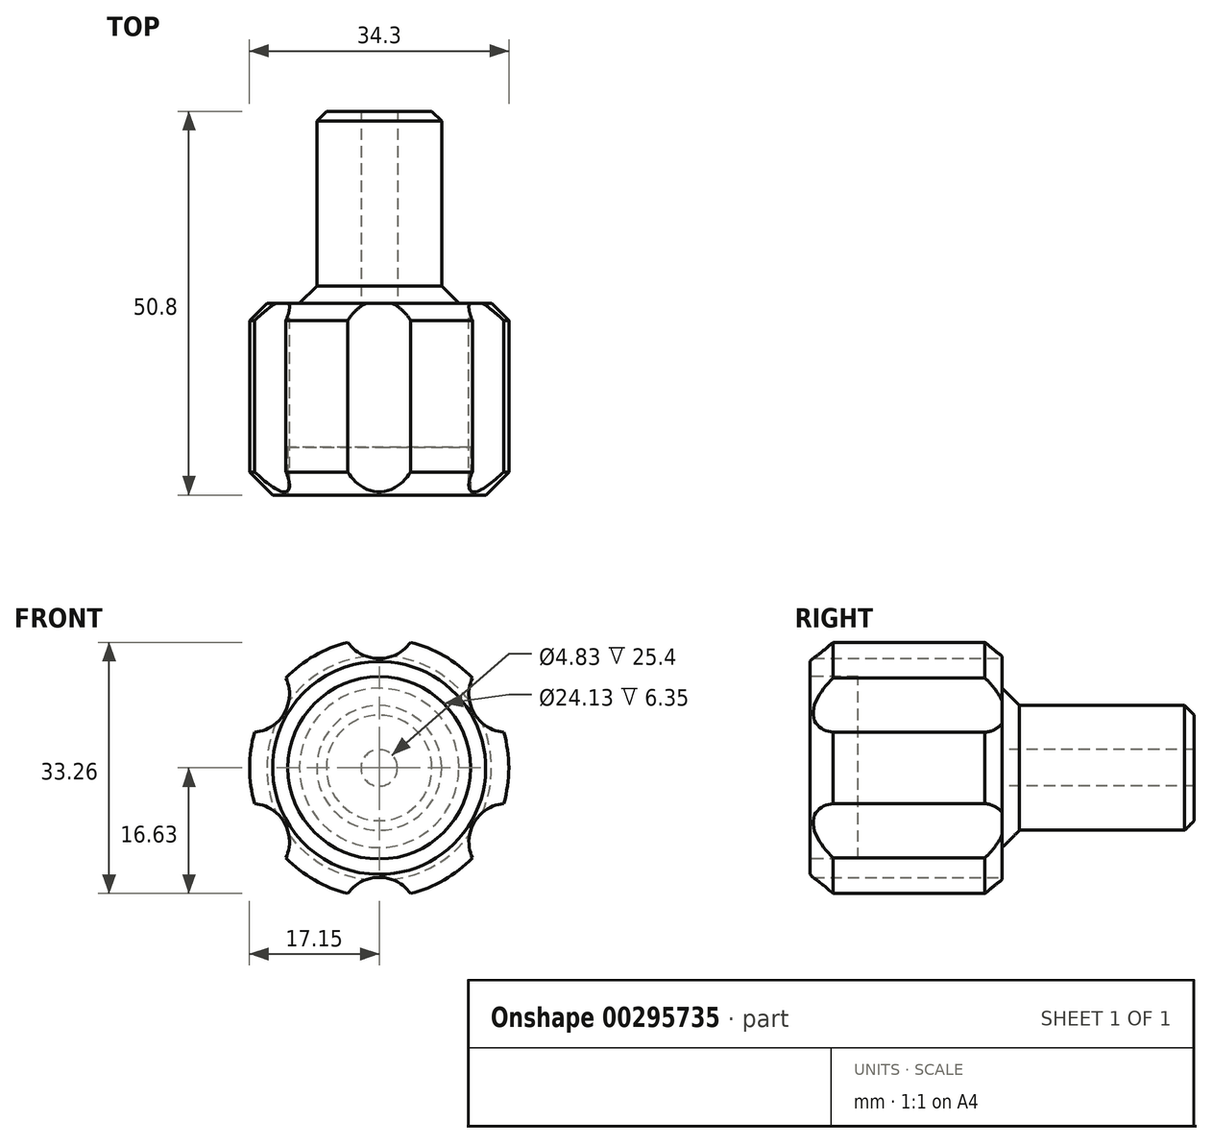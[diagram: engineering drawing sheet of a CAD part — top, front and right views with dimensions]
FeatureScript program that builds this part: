
annotation { "Feature Type Name" : "Feature", "Feature Type Description" : "" }
export const myFeature = defineFeature(function(context is Context, id is Id, definition is map)
    precondition{}
    {
        {
            var Q0;
            Q0=qCreatedBy(makeId("Front.planeOp"),FACE);
            var sketch = newSketch(context, id + "F0", { "sketchPlane" : qUnion([Q0])});
            skCircle(sketch, "E0", {"center": v(0, 0) * mm, "radius": 17.15 * mm});
            skSolve(sketch);
        }
        {
            var Q0;
            Q0=qCreatedBy(makeId("Front.planeOp"),FACE);
            var sketch = newSketch(context, id + "F1", { "sketchPlane" : qUnion([Q0])});
            skCircle(sketch, "E1", {"center": v(0, 0) * mm, "radius": 8.26 * mm});
            skSolve(sketch);
        }
        {
            var Q0;
            Q0=qCreatedBy(makeId("Front.planeOp"),FACE);
            var sketch = newSketch(context, id + "F2", { "sketchPlane" : qUnion([Q0])});
            skCircle(sketch, "E2", {"center": v(0, 0) * mm, "radius": 2.41 * mm});
            skSolve(sketch);
        }
        {
            var Q0;
            Q0=qCreatedBy(makeId("Front.planeOp"),FACE);
            cPlane(context, id + "F3", {"entities" : qUnion([Q0]), "cplaneType" : CPlaneType.OFFSET, "offset" : 25.4 * mm, "width" : 152.4 * mm, "height" : 152.4 * mm});
        }
        {
            var Q0;
            Q0=qCreatedBy(id+"F3.planeOp",FACE);
            var sketch = newSketch(context, id + "F4", { "sketchPlane" : qUnion([Q0])});
            skCircle(sketch, "E3", {"center": v(0, 0) * mm, "radius": 12.07 * mm});
            skSolve(sketch);
        }
        {
            var Q0;
            Q0 = qSketchRegion(id + "F0", true);
            extrude(context, id + "F5", {"entities" : qUnion([Q0]), "depth" : 25.4 * mm});
        }
        {
            var Q0;
            Q0=makeQuery(id+"F1.imprint","IMPRINT",FACE,{"disambiguationData":[TD([[makeQuery(id+"F1.imprint","IMPRINT",EDGE,{"derivedFrom":sQuery(id+"F1.wireOp",EDGE,"E1")}),1.0]])]});
            extrude(context, id + "F6", {"entities" : qUnion([Q0]), "operationType" : NewBodyOperationType.ADD, "oppositeDirection" : true, "depth" : 25.4 * mm});
        }
        {
            var Q0;
            Q0=makeQuery(id+"F2.imprint","IMPRINT",FACE,{"disambiguationData":[TD([[makeQuery(id+"F2.imprint","IMPRINT",EDGE,{"derivedFrom":sQuery(id+"F2.wireOp",EDGE,"E2")}),1.0]])]});
            extrude(context, id + "F7", {"entities" : qUnion([Q0]), "operationType" : NewBodyOperationType.REMOVE, "oppositeDirection" : true, "depth" : 25.4 * mm});
        }
        {
            var Q0;
            Q0=qCreatedBy(makeId("Front.planeOp"),FACE);
            var sketch = newSketch(context, id + "F8", { "sketchPlane" : qUnion([Q0])});
            skCircle(sketch, "E4", {"center": v(0, 19.56) * mm, "radius": 5.08 * mm});
            skCircle(sketch, "E5.1.0", {"center": v(-16.94, 9.78) * mm, "radius": 5.08 * mm});
            skCircle(sketch, "E5.2.0", {"center": v(-16.94, -9.78) * mm, "radius": 5.08 * mm});
            skCircle(sketch, "E5.3.0", {"center": v(0, -19.56) * mm, "radius": 5.08 * mm});
            skCircle(sketch, "E5.4.0", {"center": v(16.94, -9.78) * mm, "radius": 5.08 * mm});
            skCircle(sketch, "E5.5.0", {"center": v(16.94, 9.78) * mm, "radius": 5.08 * mm});
            skPoint(sketch, "E5.center", {"position": v(0, 0) * mm});
            skSolve(sketch);
        }
        {
            var Q0;
            Q0=makeQuery(id+"F5.opExtrude","CAP_FACE",FACE,{"disambiguationData":[OSD([sQuery(id+"F0.wireOp",EDGE,"E0")])],"isStart":false});
            chamfer(context, id + "F9", {"entities" : qUnion([Q0]), "width" : 3.05 * mm, "tangentPropagation" : true});
        }
        {
            var Q0;
            Q0=makeQuery(id+"F5.opExtrude","CAP_FACE",FACE,{"disambiguationData":[OSD([sQuery(id+"F0.wireOp",EDGE,"E0")])],"isStart":true});
            chamfer(context, id + "F10", {"entities" : qUnion([Q0]), "width" : 2.3 * mm, "tangentPropagation" : true});
        }
        {
            var Q0;
            Q0 = qSketchRegion(id + "F8", true);
            extrude(context, id + "F11", {"entities" : qUnion([Q0]), "operationType" : NewBodyOperationType.REMOVE, "depth" : 25.4 * mm});
        }
        {
            var Q0;
            Q0 = qSketchRegion(id + "F4", true);
            extrude(context, id + "F12", {"entities" : qUnion([Q0]), "operationType" : NewBodyOperationType.REMOVE, "oppositeDirection" : true, "depth" : 6.35 * mm});
        }
        {
            var Q0;
            Q0=makeQuery(id+"F6.opExtrude","CAP_EDGE",EDGE,{"disambiguationData":[OSD([sQuery(id+"F1.wireOp",EDGE,"E1")])],"isStart":false});
            chamfer(context, id + "F13", {"entities" : qUnion([Q0]), "width" : 1.27 * mm, "tangentPropagation" : true});
        }
    });
